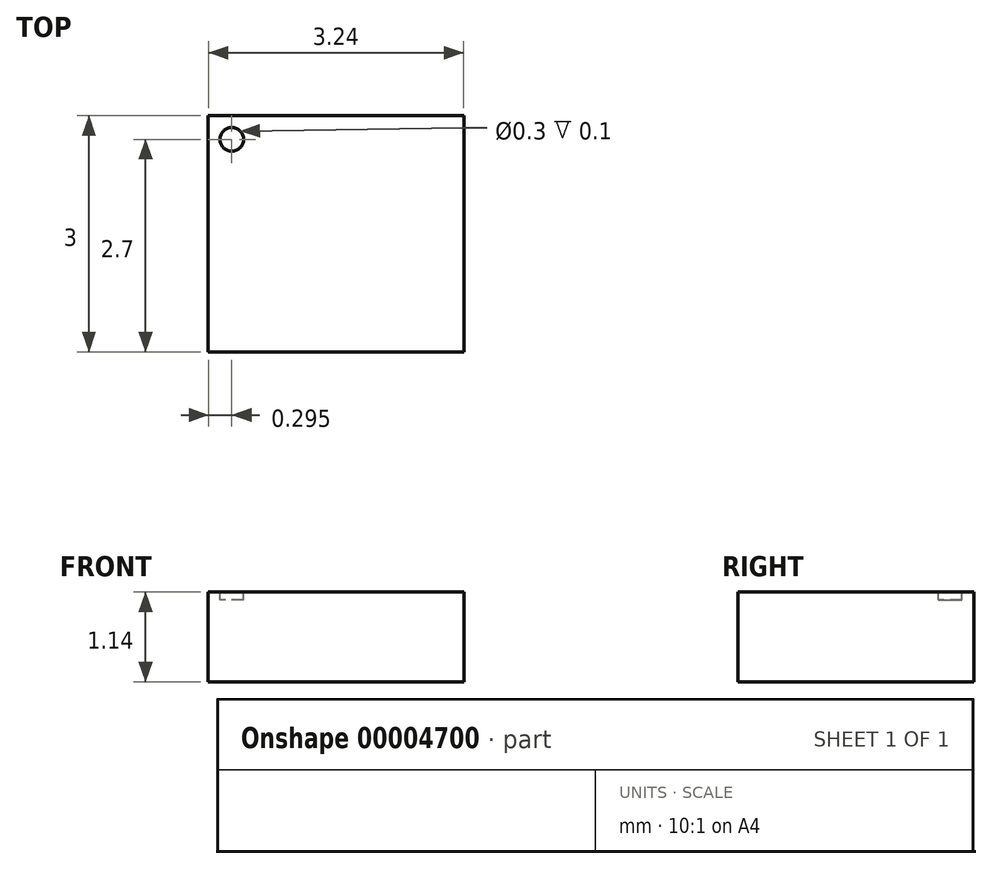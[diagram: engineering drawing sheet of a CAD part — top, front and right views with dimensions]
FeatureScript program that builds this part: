
annotation { "Feature Type Name" : "Feature", "Feature Type Description" : "" }
export const myFeature = defineFeature(function(context is Context, id is Id, definition is map)
    precondition{}
    {
        {
            var Q0;
            Q0=qCreatedBy(makeId("Top.planeOp"),FACE);
            var sketch = newSketch(context, id + "F0", { "sketchPlane" : qUnion([Q0])});
            skLineSegment(sketch, "E0.rect.bottom", {"start": v(1.62, 1.5) * mm, "end": v(-1.63, 1.5) * mm});
            skLineSegment(sketch, "E0.rect.top", {"start": v(1.63, -1.5) * mm, "end": v(-1.62, -1.5) * mm});
            skLineSegment(sketch, "E0.rect.left", {"start": v(1.62, 1.5) * mm, "end": v(1.63, -1.5) * mm});
            skLineSegment(sketch, "E0.rect.right", {"start": v(-1.63, 1.5) * mm, "end": v(-1.62, -1.5) * mm});
            skPoint(sketch, "E0.rect.middle", {"position": v(0, 0) * mm});
            skSolve(sketch);
        }
        {
            var Q0;
            Q0 = qSketchRegion(id + "F0", true);
            extrude(context, id + "F1", {"entities" : qUnion([Q0]), "depth" : 1.14 * mm});
        }
        {
            var Q0;
            Q0=makeQuery(id+"F1.opExtrude","CAP_FACE",FACE,{"disambiguationData":[OSD([sQuery(id+"F0.wireOp",EDGE,"E0.rect.bottom"),sQuery(id+"F0.wireOp",EDGE,"E0.rect.top"),sQuery(id+"F0.wireOp",EDGE,"E0.rect.left"),sQuery(id+"F0.wireOp",EDGE,"E0.rect.right")])],"isStart":false});
            var sketch = newSketch(context, id + "F2", { "sketchPlane" : qUnion([Q0])});
            skCircle(sketch, "E1", {"center": v(-1.33, 1.2) * mm, "radius": 0.15 * mm});
            skSolve(sketch);
        }
        {
            var Q0;
            Q0 = qSketchRegion(id + "F2", true);
            extrude(context, id + "F3", {"entities" : qUnion([Q0]), "operationType" : NewBodyOperationType.REMOVE, "oppositeDirection" : true, "depth" : 0.1 * mm});
        }
    });
